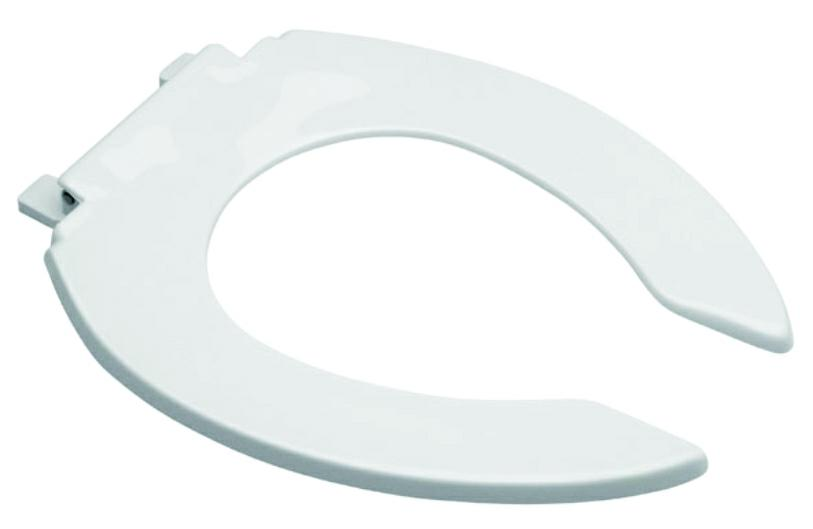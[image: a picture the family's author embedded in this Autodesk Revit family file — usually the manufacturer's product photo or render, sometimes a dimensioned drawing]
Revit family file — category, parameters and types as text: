
# Revit family: AF-1_RFA
name_source: partatom
category: Aparatos sanitarios
units: mm (PartAtom-declared; Revit-internal decimal feet)

## family parameters
Compartido = Sí
Corte con vacíos al cargar = No
Cota de conector redondo = Diámetro de uso
Número OmniClass = 23.45.00.00
Punto de cálculo de habitación = Sí
Se basa en plano de trabajo = No
Siempre vertical = Sí
Tipo de pieza = Normal
Título OmniClass = Sanitary, Laundry, and Cleaning Equipment

## types (1)
- AF-1
    Comentarios de tipo = SANIVEX
    Data Sheet = https://helvex.com.mx
    Descripción = Seat Without Lid Elongated Front Plus Open For Antibacterial Flush Valve Cup, White
    Elevación por defecto = 0"
    Fabricante = HELVEX
    Features = Glossy Finish; Antibacterial Protection
    Imagen de tipo = AF-1.jpg
    Modelo = AF-1
    Placement Height = 14.5" And 17"
    Polypropylene = Polypropylene
    Total Height = 1"
    Total Length = 18"
    Total Width = 14"
    URL = https://helvex.com.mx

## geometry (parser evidence)
native form markers: Sweep x3
no freeform markers — native parametric forms only
